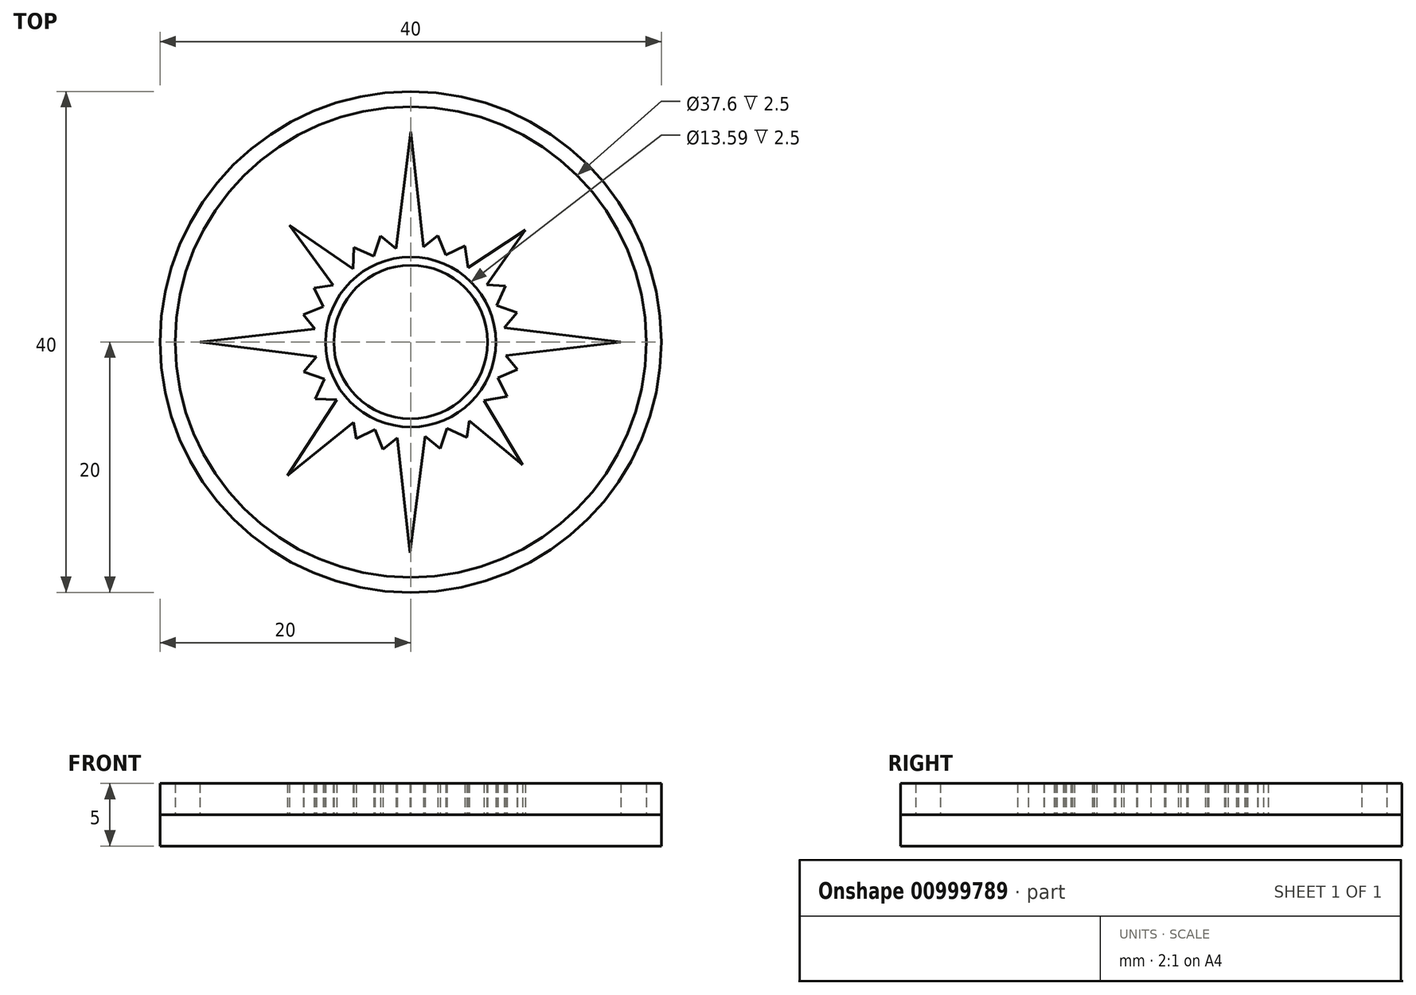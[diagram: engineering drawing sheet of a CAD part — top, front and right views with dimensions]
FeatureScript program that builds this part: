
annotation { "Feature Type Name" : "Feature", "Feature Type Description" : "" }
export const myFeature = defineFeature(function(context is Context, id is Id, definition is map)
    precondition{}
    {
        {
            var Q0;
            Q0=qCreatedBy(makeId("Top.planeOp"),FACE);
            var sketch = newSketch(context, id + "F0", { "sketchPlane" : qUnion([Q0])});
            skCircle(sketch, "E0", {"center": v(0, 0) * mm, "radius": 20 * mm});
            skCircle(sketch, "E1", {"center": v(0, 0) * mm, "radius": 18.8 * mm});
            skCircle(sketch, "E2", {"center": v(0, 0) * mm, "radius": 6.13 * mm});
            skCircle(sketch, "E3", {"center": v(0, 0) * mm, "radius": 6.8 * mm});
            skLineSegment(sketch, "E4", {"start": v(-16.8, -0.02) * mm, "end": v(-7.64, 1.04) * mm});
            skLineSegment(sketch, "E5", {"start": v(-7.64, 1.04) * mm, "end": v(-8.56, 2.17) * mm});
            skLineSegment(sketch, "E6", {"start": v(-8.56, 2.17) * mm, "end": v(-6.99, 2.83) * mm});
            skLineSegment(sketch, "E7", {"start": v(-6.99, 2.83) * mm, "end": v(-7.72, 4.33) * mm});
            skLineSegment(sketch, "E8", {"start": v(-7.72, 4.33) * mm, "end": v(-6.17, 4.53) * mm});
            skLineSegment(sketch, "E9", {"start": v(-6.17, 4.53) * mm, "end": v(-9.68, 9.34) * mm});
            skLineSegment(sketch, "E10", {"start": v(-9.68, 9.34) * mm, "end": v(-4.6, 5.84) * mm});
            skLineSegment(sketch, "E11", {"start": v(-4.6, 5.84) * mm, "end": v(-4.52, 7.56) * mm});
            skLineSegment(sketch, "E12", {"start": v(-4.52, 7.56) * mm, "end": v(-2.93, 6.87) * mm});
            skLineSegment(sketch, "E13", {"start": v(-2.93, 6.87) * mm, "end": v(-2.4, 8.47) * mm});
            skLineSegment(sketch, "E14", {"start": v(-2.4, 8.47) * mm, "end": v(-1.17, 7.47) * mm});
            skLineSegment(sketch, "E15", {"start": v(-1.17, 7.47) * mm, "end": v(0, 16.8) * mm});
            skLineSegment(sketch, "E16", {"start": v(0, 16.8) * mm, "end": v(1.04, 7.6) * mm});
            skLineSegment(sketch, "E17", {"start": v(1.04, 7.6) * mm, "end": v(2.16, 8.5) * mm});
            skLineSegment(sketch, "E18", {"start": v(2.16, 8.5) * mm, "end": v(2.82, 6.95) * mm});
            skLineSegment(sketch, "E19", {"start": v(2.82, 6.95) * mm, "end": v(4.33, 7.68) * mm});
            skLineSegment(sketch, "E20", {"start": v(4.33, 7.68) * mm, "end": v(4.58, 5.95) * mm});
            skLineSegment(sketch, "E21", {"start": v(4.58, 5.95) * mm, "end": v(9.17, 8.95) * mm});
            skLineSegment(sketch, "E22", {"start": v(9.17, 8.95) * mm, "end": v(6.08, 4.57) * mm});
            skLineSegment(sketch, "E23", {"start": v(6.08, 4.57) * mm, "end": v(7.56, 4.48) * mm});
            skLineSegment(sketch, "E24", {"start": v(7.56, 4.48) * mm, "end": v(6.86, 2.91) * mm});
            skLineSegment(sketch, "E25", {"start": v(6.86, 2.91) * mm, "end": v(8.49, 2.34) * mm});
            skLineSegment(sketch, "E26", {"start": v(8.49, 2.34) * mm, "end": v(7.48, 1.14) * mm});
            skLineSegment(sketch, "E27", {"start": v(7.48, 1.14) * mm, "end": v(16.78, -0.02) * mm});
            skLineSegment(sketch, "E28", {"start": v(16.78, -0.02) * mm, "end": v(7.6, -1.1) * mm});
            skLineSegment(sketch, "E29", {"start": v(7.6, -1.1) * mm, "end": v(8.5, -2.19) * mm});
            skLineSegment(sketch, "E30", {"start": v(8.5, -2.19) * mm, "end": v(6.97, -2.86) * mm});
            skLineSegment(sketch, "E31", {"start": v(6.97, -2.86) * mm, "end": v(7.68, -4.34) * mm});
            skLineSegment(sketch, "E32", {"start": v(7.68, -4.34) * mm, "end": v(5.86, -4.69) * mm});
            skLineSegment(sketch, "E33", {"start": v(5.86, -4.69) * mm, "end": v(8.94, -9.8) * mm});
            skLineSegment(sketch, "E34", {"start": v(8.94, -9.8) * mm, "end": v(4.67, -6.3) * mm});
            skLineSegment(sketch, "E35", {"start": v(4.67, -6.3) * mm, "end": v(4.5, -7.62) * mm});
            skLineSegment(sketch, "E36", {"start": v(4.5, -7.62) * mm, "end": v(2.9, -6.9) * mm});
            skLineSegment(sketch, "E37", {"start": v(2.9, -6.9) * mm, "end": v(2.37, -8.52) * mm});
            skLineSegment(sketch, "E38", {"start": v(2.37, -8.52) * mm, "end": v(1.14, -7.52) * mm});
            skLineSegment(sketch, "E39", {"start": v(1.14, -7.52) * mm, "end": v(-0.04, -16.83) * mm});
            skLineSegment(sketch, "E40", {"start": v(-0.04, -16.83) * mm, "end": v(-1.07, -7.64) * mm});
            skLineSegment(sketch, "E41", {"start": v(-1.07, -7.64) * mm, "end": v(-2.2, -8.56) * mm});
            skLineSegment(sketch, "E42", {"start": v(-2.2, -8.56) * mm, "end": v(-2.85, -7) * mm});
            skLineSegment(sketch, "E43", {"start": v(-2.85, -7) * mm, "end": v(-4.35, -7.73) * mm});
            skLineSegment(sketch, "E44", {"start": v(-4.35, -7.73) * mm, "end": v(-4.58, -6.42) * mm});
            skLineSegment(sketch, "E45", {"start": v(-4.58, -6.42) * mm, "end": v(-9.83, -10.67) * mm});
            skLineSegment(sketch, "E46", {"start": v(-9.83, -10.67) * mm, "end": v(-5.89, -4.62) * mm});
            skLineSegment(sketch, "E47", {"start": v(-5.89, -4.62) * mm, "end": v(-7.61, -4.54) * mm});
            skLineSegment(sketch, "E48", {"start": v(-7.61, -4.54) * mm, "end": v(-6.9, -2.94) * mm});
            skLineSegment(sketch, "E49", {"start": v(-6.9, -2.94) * mm, "end": v(-8.53, -2.37) * mm});
            skLineSegment(sketch, "E50", {"start": v(-8.53, -2.37) * mm, "end": v(-7.5, -1.17) * mm});
            skLineSegment(sketch, "E51", {"start": v(-7.5, -1.17) * mm, "end": v(-16.8, -0.02) * mm});
            skSolve(sketch);
        }
        {
            var Q0;
            Q0=makeQuery(id+"F0.imprint","IMPRINT",FACE,{"disambiguationData":[TD([[makeQuery(id+"F0.imprint","IMPRINT",EDGE,{"derivedFrom":sQuery(id+"F0.wireOp",EDGE,"E2")}),1.0]])]});
            var Q1;
            Q1=makeQuery(id+"F0.imprint","IMPRINT",FACE,{"disambiguationData":[TD([[makeQuery(id+"F0.imprint","IMPRINT",EDGE,{"derivedFrom":sQuery(id+"F0.wireOp",EDGE,"E3")}),-1.0]])]});
            var Q2;
            Q2=makeQuery(id+"F0.imprint","IMPRINT",FACE,{"disambiguationData":[TD([[makeQuery(id+"F0.imprint","IMPRINT",EDGE,{"derivedFrom":sQuery(id+"F0.wireOp",EDGE,"E0")}),1.0]])]});
            extrude(context, id + "F1", {"entities" : qUnion([Q0, Q1, Q2]), "depth" : 2.5 * mm, "offsetDistance" : 25 * mm});
        }
        {
            var Q0;
            Q0=makeQuery(id+"F0.imprint","IMPRINT",FACE,{"disambiguationData":[TD([[makeQuery(id+"F0.imprint","IMPRINT",EDGE,{"derivedFrom":sQuery(id+"F0.wireOp",EDGE,"E0")}),1.0]])]});
            var Q1;
            Q1=makeQuery(id+"F0.imprint","IMPRINT",FACE,{"disambiguationData":[TD([[makeQuery(id+"F0.imprint","IMPRINT",EDGE,{"derivedFrom":sQuery(id+"F0.wireOp",EDGE,"E1")}),1.0]])]});
            var Q2;
            Q2=makeQuery(id+"F0.imprint","IMPRINT",FACE,{"disambiguationData":[TD([[makeQuery(id+"F0.imprint","IMPRINT",EDGE,{"derivedFrom":sQuery(id+"F0.wireOp",EDGE,"E3")}),-1.0]])]});
            var Q3;
            Q3=makeQuery(id+"F0.imprint","IMPRINT",FACE,{"disambiguationData":[TD([[makeQuery(id+"F0.imprint","IMPRINT",EDGE,{"derivedFrom":sQuery(id+"F0.wireOp",EDGE,"E2")}),1.0]])]});
            var Q4;
            Q4=makeQuery(id+"F0.imprint","IMPRINT",FACE,{"disambiguationData":[TD([[makeQuery(id+"F0.imprint","IMPRINT",EDGE,{"derivedFrom":sQuery(id+"F0.wireOp",EDGE,"E2")}),-1.0]])]});
            extrude(context, id + "F2", {"entities" : qUnion([Q0, Q1, Q2, Q3, Q4]), "oppositeDirection" : true, "depth" : 2.5 * mm, "offsetDistance" : 25 * mm});
        }
    });
